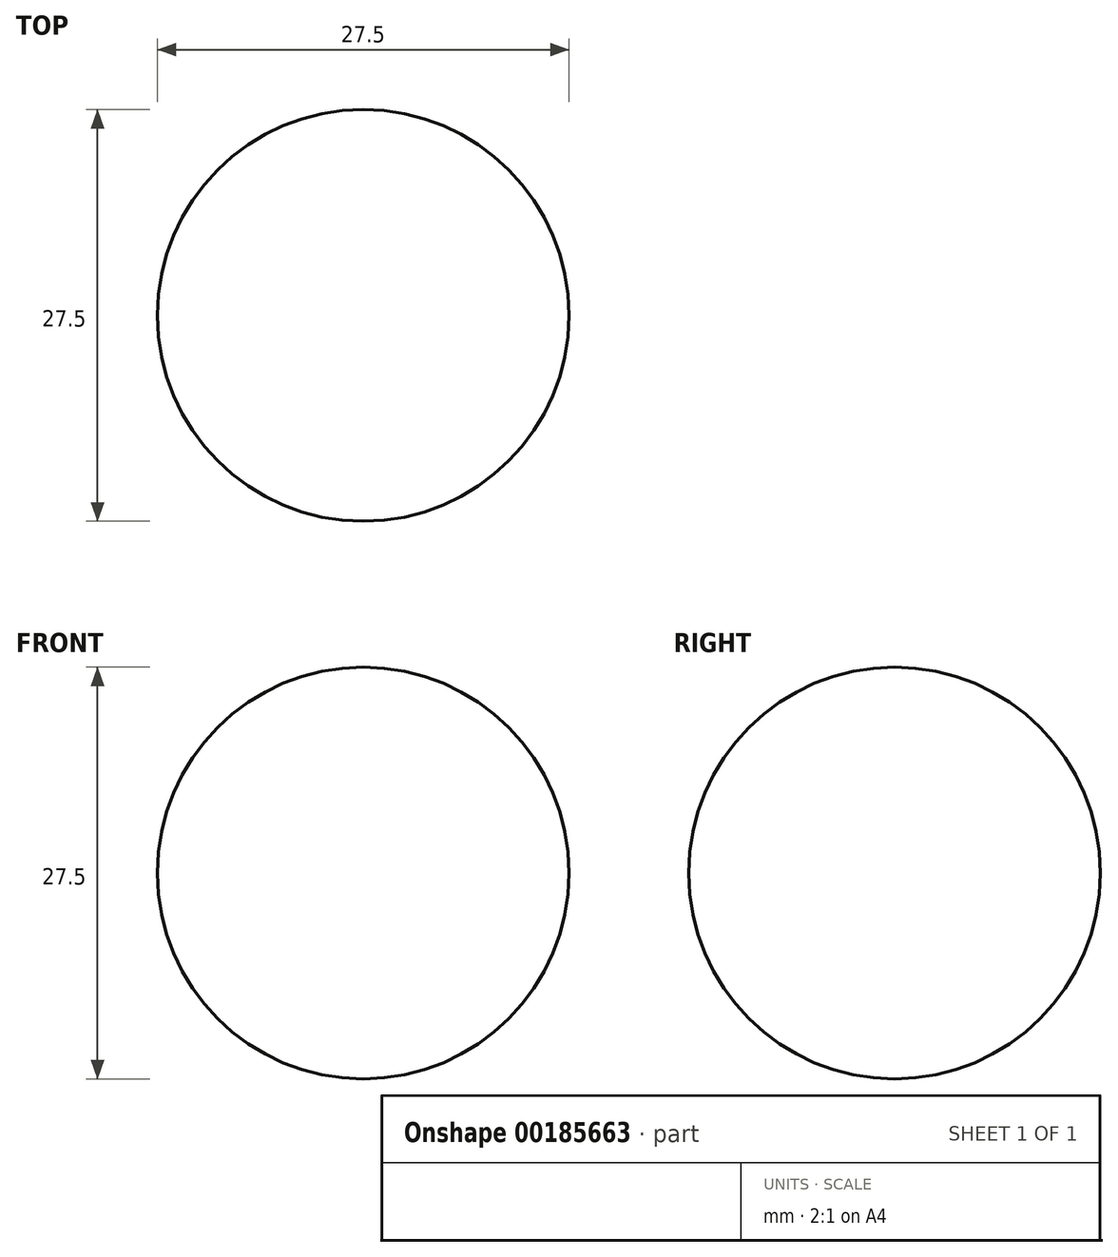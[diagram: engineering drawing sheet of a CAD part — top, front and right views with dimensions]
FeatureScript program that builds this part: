
annotation { "Feature Type Name" : "Feature", "Feature Type Description" : "" }
export const myFeature = defineFeature(function(context is Context, id is Id, definition is map)
    precondition{}
    {
        {
            var Q0;
            Q0=qCreatedBy(makeId("Top.planeOp"),FACE);
            var sketch = newSketch(context, id + "F0", { "sketchPlane" : qUnion([Q0])});
            skCircle(sketch, "E0", {"center": v(0, 0) * mm, "radius": 13.75 * mm});
            skLineSegment(sketch, "E1", {"start": v(0, -13.75) * mm, "end": v(0, 13.75) * mm});
            skSolve(sketch);
        }
        {
            var Q0;
            {var subQ0=sQuery(id+"F0.wireOp",EDGE,"E1");Q0=makeQuery(id+"F0.imprint","IMPRINT",FACE,{"disambiguationData":[TD([[makeQuery(id+"F0.imprint","IMPRINT",EDGE,{"derivedFrom":subQ0}),1.0]])]});}
            var Q1;
            Q1=sQuery(id+"F0.wireOp",EDGE,"E1");
            revolve(context, id + "F1", {"entities" : qUnion([Q0]), "axis" : qUnion([Q1]), "revolveType" : RevolveType.FULL});
        }
    });
